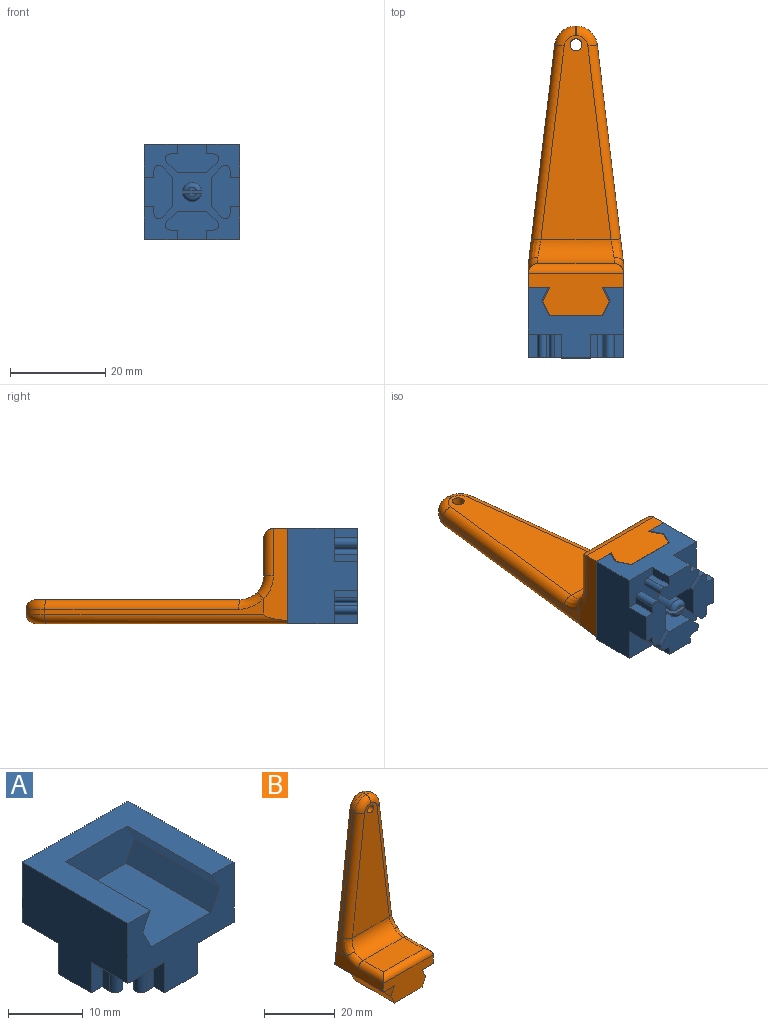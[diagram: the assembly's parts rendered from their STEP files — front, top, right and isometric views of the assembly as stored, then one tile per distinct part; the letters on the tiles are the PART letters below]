
ASSEMBLY  parts=2 mates=1
PART A: 60 faces, bbox 20x20x14.8 mm
  f0: cylinder r=2mm len=4mm, axis (0,0,1), area 21.9mm2, adj f2,f48,f59
  f1: plane 1.83x0.6mm, normal (0,0,-1), area 0.8mm2, adj f49,f58
  f2: plane 20x20mm, normal (0,0,-1), area 193.3mm2, adj f0,f4,f5,f6,f7,f14,f15,f16
  f3: plane 20x20mm, normal (0,0,1), area 213.6mm2, adj f4,f5,f6,f7,f8,f9,f10
  f4: plane 20x14.8mm, normal (0,-1,0), area 149.4mm2, adj f2,f3,f5,f6,f9,f10,f11,f12
  f5: plane 20x14.8mm, normal (-1,0,0), area 227mm2, adj f2,f3,f4,f7,f15,f16,f21
  f6: plane 20x14.8mm, normal (1,0,0), area 227mm2, adj f2,f3,f4,f7,f32,f38,f39
  f7: plane 20x14.8mm, normal (0,1,0), area 227mm2, adj f2,f3,f5,f6,f24,f30,f31
  f8: plane 14.45x6mm, normal (0,-1,0), area 77.6mm2, adj f3,f9,f10,f11,f12,f13
  f9: plane 16x2.8mm, normal (-0.89,0,-0.45), area 50.1mm2, adj f3,f4,f8,f11
  f10: plane 16x2.8mm, normal (0.89,0,-0.45), area 50.1mm2, adj f3,f4,f8,f12
  f11: plane 16x3.2mm, normal (-0.89,0,0.45), area 57.2mm2, adj f4,f8,f9,f13
  f12: plane 16x3.2mm, normal (0.89,0,0.45), area 57.2mm2, adj f4,f8,f10,f13
  f13: plane 16x11.25mm, normal (0,0,1), area 180mm2, adj f4,f8,f11,f12
  f14: plane 5x1.49mm, normal (-1,0,0), area 7.4mm2, adj f2,f15,f21,f56
  f15: plane 5x2mm, normal (0,-1,0), area 10mm2, adj f2,f5,f14,f21
  f16: plane 5x2mm, normal (0,1,0), area 10mm2, adj f2,f5,f17,f21
  f17: plane 5x1.49mm, normal (-1,0,0), area 7.4mm2, adj f2,f16,f21,f57
  f18: plane 5x2.19mm, normal (0.71,0.71,0), area 15.5mm2, adj f2,f19,f21,f57
  f19: plane 6.2x5mm, normal (1,0,0), area 31mm2, adj f2,f18,f20,f21
  f20: plane 5x2.19mm, normal (0.71,-0.71,0), area 15.5mm2, adj f2,f19,f21,f56
  f21: plane 11.17x5.9mm, normal (0,0,-1), area 49.3mm2, adj f5,f14,f15,f16,f17,f18,f19,f20
  f22: cylinder r=2mm len=4mm, axis (0,0,1), area 21.9mm2, adj f2,f49,f58
  f23: plane 1.83x0.6mm, normal (0,0,-1), area 0.8mm2, adj f48,f59
  f24: plane 5x2mm, normal (1,0,0), area 10mm2, adj f2,f7,f25,f31
  f25: plane 5x1.49mm, normal (0,1,0), area 7.4mm2, adj f2,f24,f31,f55
  f26: plane 5x2.19mm, normal (0.71,-0.71,0), area 15.5mm2, adj f2,f27,f31,f55
  f27: plane 6.2x5mm, normal (0,-1,0), area 31mm2, adj f2,f26,f28,f31
  f28: plane 5x2.19mm, normal (-0.71,-0.71,0), area 15.5mm2, adj f2,f27,f31,f54
  f29: plane 5x1.49mm, normal (0,1,0), area 7.4mm2, adj f2,f30,f31,f54
  f30: plane 5x2mm, normal (-1,0,0), area 10mm2, adj f2,f7,f29,f31
  f31: plane 11.17x5.9mm, normal (0,0,-1), area 49.3mm2, adj f7,f24,f25,f26,f27,f28,f29,f30
  f32: plane 5x2mm, normal (0,-1,0), area 10mm2, adj f2,f6,f33,f39
  f33: plane 5x1.49mm, normal (1,0,0), area 7.4mm2, adj f2,f32,f39,f53
  f34: plane 5x2.19mm, normal (-0.71,-0.71,0), area 15.5mm2, adj f2,f35,f39,f53
  f35: plane 6.2x5mm, normal (-1,0,0), area 31mm2, adj f2,f34,f36,f39
  f36: plane 5x2.19mm, normal (-0.71,0.71,0), area 15.5mm2, adj f2,f35,f39,f52
  f37: plane 5x1.49mm, normal (1,0,0), area 7.4mm2, adj f2,f38,f39,f52
  f38: plane 5x2mm, normal (0,1,0), area 10mm2, adj f2,f6,f37,f39
  f39: plane 11.17x5.9mm, normal (0,0,-1), area 49.3mm2, adj f6,f32,f33,f34,f35,f36,f37,f38
  f40: plane 5x2mm, normal (-1,0,0), area 10mm2, adj f2,f4,f41,f47
  f41: plane 5x1.49mm, normal (0,-1,0), area 7.4mm2, adj f2,f40,f47,f51
  f42: plane 5x2.19mm, normal (-0.71,0.71,0), area 15.5mm2, adj f2,f43,f47,f51
  f43: plane 6.2x5mm, normal (0,1,0), area 31mm2, adj f2,f42,f44,f47
  f44: plane 5x2.19mm, normal (0.71,0.71,0), area 15.5mm2, adj f2,f43,f47,f50
  f45: plane 5x1.49mm, normal (0,-1,0), area 7.4mm2, adj f2,f46,f47,f50
  f46: plane 5x2mm, normal (1,0,0), area 10mm2, adj f2,f4,f45,f47
  f47: plane 11.17x5.9mm, normal (0,0,-1), area 49.3mm2, adj f4,f40,f41,f42,f43,f44,f45,f46
  f48: plane 5x3.92mm, normal (0,1,0), area 19.2mm2, adj f0,f2,f23,f59
  f49: plane 5x3.92mm, normal (0,-1,0), area 19.2mm2, adj f1,f2,f22,f58
  f50: cylinder r=1mm len=5mm, axis (0,0,-1), area 11.8mm2, adj f2,f44,f45,f47
  f51: cylinder r=1mm len=5mm, axis (0,0,1), area 11.8mm2, adj f2,f41,f42,f47
  f52: cylinder r=1mm len=5mm, axis (0,0,-1), area 11.8mm2, adj f2,f36,f37,f39
  f53: cylinder r=1mm len=5mm, axis (0,0,1), area 11.8mm2, adj f2,f33,f34,f39
  f54: cylinder r=1mm len=5mm, axis (0,0,-1), area 11.8mm2, adj f2,f28,f29,f31
  f55: cylinder r=1mm len=5mm, axis (0,0,1), area 11.8mm2, adj f2,f25,f26,f31
  f56: cylinder r=1mm len=5mm, axis (0,0,-1), area 11.8mm2, adj f2,f14,f20,f21
  f57: cylinder r=1mm len=5mm, axis (0,0,1), area 11.8mm2, adj f2,f17,f18,f21
  f58: torus R=1mm, axis (0,0,-1), area 6.8mm2, adj f1,f22,f49
  f59: torus R=1mm, axis (0,0,-1), area 6.8mm2, adj f0,f23,f48
PART B: 39 faces, bbox 21.2x20x61.4 mm
  f0: cylinder r=1.25mm len=2.5mm, axis (0,-1,0), area 19.6mm2, adj f15,f19
  f1: plane 16x11mm, normal (0,0,-1), area 176mm2, adj f2,f3,f4,f5
  f2: plane 16x3mm, normal (0.89,0,-0.45), area 53.7mm2, adj f1,f3,f5,f6
  f3: plane 14x6mm, normal (0,1,0), area 75mm2, adj f1,f2,f4,f6,f7,f8
  f4: plane 16x3mm, normal (-0.89,0,-0.45), area 53.7mm2, adj f1,f3,f5,f7
  f5: plane 20x9mm, normal (0,-1,0), area 135mm2, adj f1,f2,f4,f6,f7,f8,f9,f11
  f6: plane 16x3mm, normal (0.89,0,0.45), area 53.7mm2, adj f2,f3,f5,f8
  f7: plane 16x3mm, normal (-0.89,0,0.45), area 53.7mm2, adj f3,f4,f5,f8
  f8: plane 20.01x20.01mm, normal (0,0,-1), area 223.5mm2, adj f3,f5,f6,f7,f9,f10,f11,f34
  f9: plane 19.42x5mm, normal (1,0,0), area 68.2mm2, adj f5,f8,f16,f23,f25,f34
  f10: plane 53x17.17mm, normal (0,1,0), area 562.4mm2, adj f8,f20,f34,f35,f36,f37,f38
  f11: plane 19.42x5mm, normal (-1,0,0), area 68.2mm2, adj f5,f8,f14,f29,f31,f38
  f12: plane 16x8mm, normal (0,0,1), area 128mm2, adj f21,f25,f27,f29
  f13: plane 1x0.02mm, normal (0,0,1), area 0mm2, adj f17,f18,f28,f36
  f14: plane 46.08x5.56mm, normal (-0.99,0,0.12), area 50.2mm2, adj f11,f18,f31,f32,f33,f38
  f15: plane 43x14.77mm, normal (0,-1,0), area 406.4mm2, adj f0,f21,f24,f26,f28,f30,f32
  f16: plane 46.08x5.56mm, normal (0.99,0,0.12), area 50.2mm2, adj f9,f17,f22,f23,f24,f34
  f17: cylinder r=4.5mm len=4.47mm, axis (0,1,0), area 6.5mm2, adj f13,f16,f26,f35
  f18: cylinder r=4.5mm len=4.47mm, axis (0,1,0), area 6.5mm2, adj f13,f14,f30,f37
  f19: plane 3.3x3.3mm, normal (0,1,0), area 3.6mm2, adj f0,f20
  f20: cylinder r=1.65mm len=3.3mm, axis (0,1,0), area 25.9mm2, adj f10,f19
  f21: cylinder r=5mm len=16mm, axis (-1,0,0), area 123.1mm2, adj f12,f15,f22,f23,f31,f33
  f22: bspline ~5.18x3.63mm, area 14.6mm2, adj f16,f21,f23,f24
  f23: torus R=7mm, axis (-1,0,0), area 13.7mm2, adj f9,f16,f21,f22,f25
  f24: cylinder r=2mm len=41.04mm, axis (-0.12,0,0.99), area 129.1mm2, adj f15,f16,f22,f26
  f25: cylinder r=2mm len=10mm, axis (0,-1,0), area 28.3mm2, adj f9,f12,f23,f27
  f26: torus R=2.5mm, axis (0,-1,0), area 17.2mm2, adj f15,f17,f24,f28
  f27: cylinder r=2mm len=20mm, axis (-1,0,0), area 56.5mm2, adj f5,f12,f25,f29
  f28: cylinder r=2mm len=2mm, axis (1,0,0), area 0mm2, adj f13,f15,f26,f30
  f29: cylinder r=2mm len=10mm, axis (0,1,0), area 28.3mm2, adj f11,f12,f27,f31
  f30: torus R=2.5mm, axis (0,-1,0), area 17.2mm2, adj f15,f18,f28,f32
  f31: torus R=7mm, axis (-1,0,0), area 13.7mm2, adj f11,f14,f21,f29,f33
  f32: cylinder r=2mm len=41.04mm, axis (-0.12,0,-0.99), area 129.1mm2, adj f14,f15,f30,f33
  f33: bspline ~5.18x3.63mm, area 14.6mm2, adj f14,f21,f31,f32
  f34: cylinder r=2mm len=51.2mm, axis (-0.12,0,0.99), area 155.9mm2, adj f8,f9,f10,f16,f35
  f35: torus R=2.5mm, axis (0,1,0), area 17.2mm2, adj f10,f17,f34,f36
  f36: cylinder r=2mm len=2mm, axis (-1,0,0), area 0mm2, adj f10,f13,f35,f37
  f37: torus R=2.5mm, axis (0,1,0), area 17.2mm2, adj f10,f18,f36,f38
  f38: cylinder r=2mm len=51.2mm, axis (-0.12,0,-0.99), area 155.9mm2, adj f8,f10,f11,f14,f37
PLACE A rot(axis=(-1,0,0),90deg) t=(-50.08,-5.13,38.41)mm fixed
PLACE B rot(axis=(-1,0,0),90deg) t=(-50.08,-5.31,38.41)mm
MATE parallel A.f8 <-> B.f3  axis (0,0,1) through (-50.08,-2.31,30.41)mm
